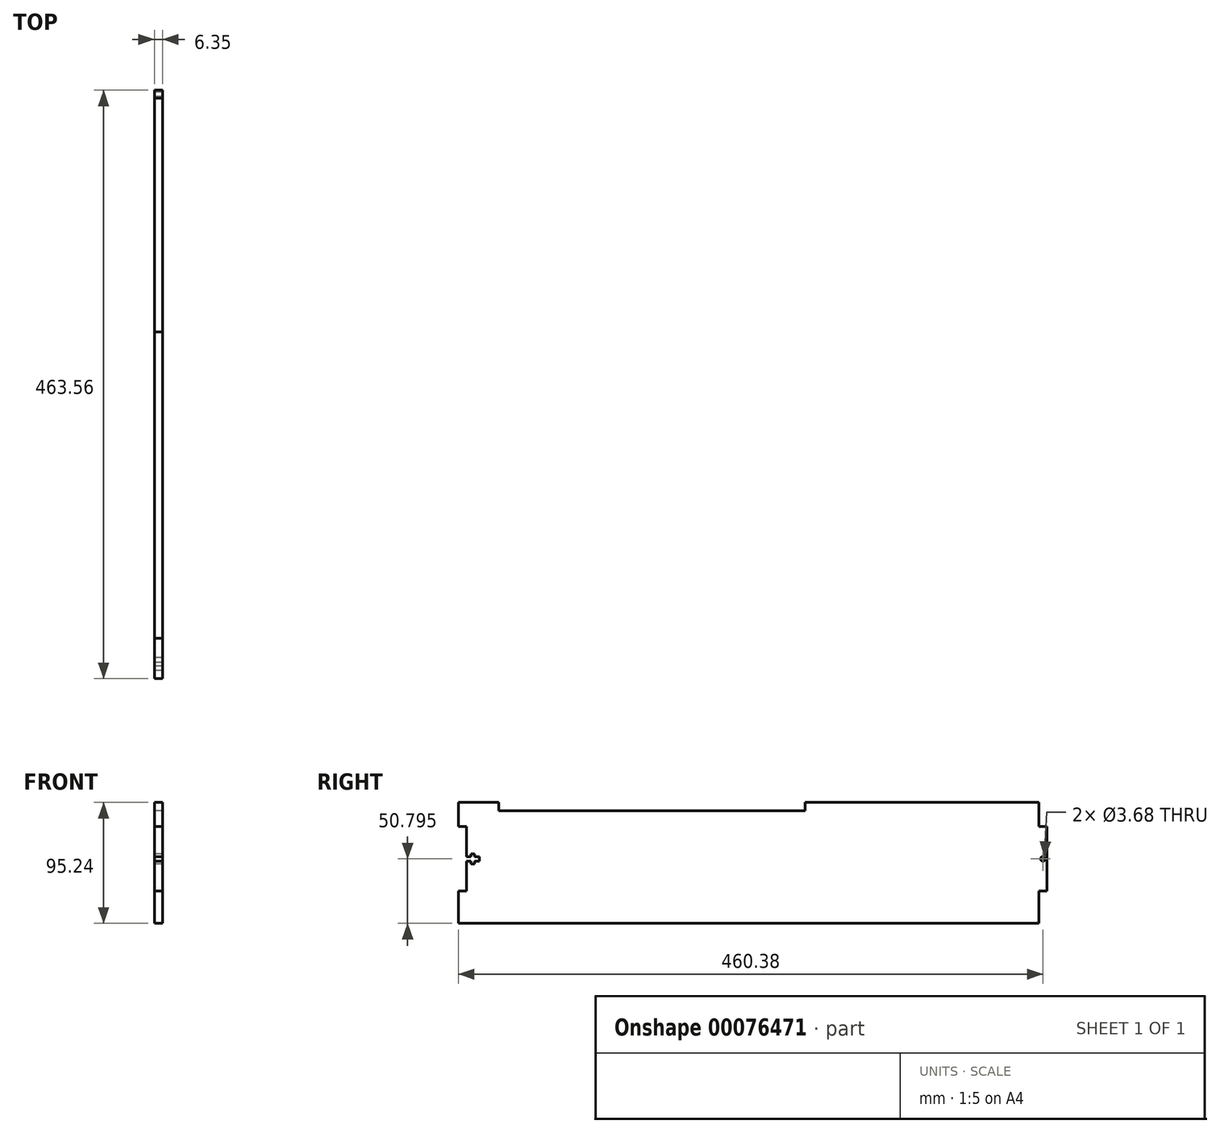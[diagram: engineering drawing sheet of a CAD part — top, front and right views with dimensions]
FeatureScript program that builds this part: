
annotation { "Feature Type Name" : "Feature", "Feature Type Description" : "" }
export const myFeature = defineFeature(function(context is Context, id is Id, definition is map)
    precondition{}
    {
        {
            var Q0;
            Q0=qCreatedBy(makeId("Right.planeOp"),FACE);
            var sketch = newSketch(context, id + "F0", { "sketchPlane" : qUnion([Q0])});
            skLineSegment(sketch, "E0.bottom", {"start": v(231.78, 47.63) * mm, "end": v(-231.78, 47.62) * mm});
            skLineSegment(sketch, "E0.top", {"start": v(231.78, -47.62) * mm, "end": v(-231.78, -47.63) * mm});
            skLineSegment(sketch, "E0.left", {"start": v(231.78, 47.63) * mm, "end": v(231.78, -47.62) * mm});
            skLineSegment(sketch, "E0.right", {"start": v(-231.78, 47.62) * mm, "end": v(-231.77, -47.63) * mm});
            skPoint(sketch, "E0.middle", {"position": v(0, 0) * mm});
            skSolve(sketch);
        }
        {
            var Q0;
            Q0=makeQuery(id+"F0.imprint","IMPRINT",FACE,{"disambiguationData":[TD([[makeQuery(id+"F0.imprint","IMPRINT",EDGE,{"derivedFrom":sQuery(id+"F0.wireOp",EDGE,"E0.bottom")}),1.0]])]});
            extrude(context, id + "F1", {"entities" : qUnion([Q0]), "depth" : 6.35 * mm});
        }
        {
            var Q0;
            Q0=qCreatedBy(makeId("Right.planeOp"),FACE);
            var sketch = newSketch(context, id + "F2", { "sketchPlane" : qUnion([Q0])});
            skLineSegment(sketch, "E1.bottom", {"start": v(-231.78, 28.57) * mm, "end": v(-225.43, 28.57) * mm});
            skLineSegment(sketch, "E1.top", {"start": v(-231.78, -22.23) * mm, "end": v(-225.43, -22.23) * mm});
            skLineSegment(sketch, "E1.left", {"start": v(-231.78, 28.57) * mm, "end": v(-231.78, -22.23) * mm});
            skLineSegment(sketch, "E1.right", {"start": v(-225.43, 28.57) * mm, "end": v(-225.43, -22.23) * mm});
            skLineSegment(sketch, "E2.bottom", {"start": v(225.43, 47.62) * mm, "end": v(231.78, 47.62) * mm});
            skLineSegment(sketch, "E2.top", {"start": v(225.43, 28.57) * mm, "end": v(231.78, 28.57) * mm});
            skLineSegment(sketch, "E2.left", {"start": v(225.43, 47.63) * mm, "end": v(225.43, 28.58) * mm});
            skLineSegment(sketch, "E2.right", {"start": v(231.78, 47.63) * mm, "end": v(231.78, 28.58) * mm});
            skLineSegment(sketch, "E3.bottom", {"start": v(225.43, -22.23) * mm, "end": v(231.78, -22.23) * mm});
            skLineSegment(sketch, "E3.top", {"start": v(225.43, -47.63) * mm, "end": v(231.78, -47.63) * mm});
            skLineSegment(sketch, "E3.left", {"start": v(225.43, -22.22) * mm, "end": v(225.43, -47.62) * mm});
            skLineSegment(sketch, "E3.right", {"start": v(231.78, -22.22) * mm, "end": v(231.78, -47.62) * mm});
            skCircle(sketch, "E4", {"center": v(228.6, 3.18) * mm, "radius": 1.84 * mm});
            skLineSegment(sketch, "E5.bottom", {"start": v(-215.27, 1.33) * mm, "end": v(-225.43, 1.33) * mm});
            skLineSegment(sketch, "E5.top", {"start": v(-215.27, 5.02) * mm, "end": v(-225.43, 5.02) * mm});
            skLineSegment(sketch, "E5.left", {"start": v(-215.27, 1.33) * mm, "end": v(-215.27, 5.02) * mm});
            skLineSegment(sketch, "E5.right", {"start": v(-225.43, 1.33) * mm, "end": v(-225.43, 5.02) * mm});
            skPoint(sketch, "E5.middle", {"position": v(-220.35, 3.17) * mm});
            skLineSegment(sketch, "E6.bottom", {"start": v(-218.92, 7.11) * mm, "end": v(-221.77, 7.11) * mm});
            skLineSegment(sketch, "E6.top", {"start": v(-218.92, -0.76) * mm, "end": v(-221.77, -0.76) * mm});
            skLineSegment(sketch, "E6.left", {"start": v(-218.92, 7.11) * mm, "end": v(-218.92, -0.76) * mm});
            skLineSegment(sketch, "E6.right", {"start": v(-221.77, 7.11) * mm, "end": v(-221.77, -0.76) * mm});
            skLineSegment(sketch, "E7.bottom", {"start": v(-200.03, 47.63) * mm, "end": v(41.27, 47.63) * mm});
            skLineSegment(sketch, "E7.top", {"start": v(-200.03, 41.15) * mm, "end": v(41.27, 41.15) * mm});
            skLineSegment(sketch, "E7.left", {"start": v(-200.03, 47.63) * mm, "end": v(-200.03, 41.15) * mm});
            skLineSegment(sketch, "E7.right", {"start": v(41.27, 47.63) * mm, "end": v(41.27, 41.15) * mm});
            skSolve(sketch);
        }
        {
            var Q0;
            Q0 = qSketchRegion(id + "F2", true);
            extrude(context, id + "F3", {"entities" : qUnion([Q0]), "operationType" : NewBodyOperationType.REMOVE, "depth" : 25.4 * mm});
        }
        {
            var Q0;
            Q0=makeQuery(id+"F1.opExtrude","SWEPT_BODY",BODY,{"disambiguationData":[OSD([sQuery(id+"F0.wireOp",EDGE,"E0.bottom"),sQuery(id+"F0.wireOp",EDGE,"E0.top"),sQuery(id+"F0.wireOp",EDGE,"E0.left"),sQuery(id+"F0.wireOp",EDGE,"E0.right")])]});
            transform(context, id + "F4", {"entities" : qUnion([Q0]), "transformType" : TransformType.TRANSLATION_3D, "dx" : 0 * mm, "dy" : 0 * mm, "dz" : 0 * mm, "makeCopy" : true});
        }
    });
